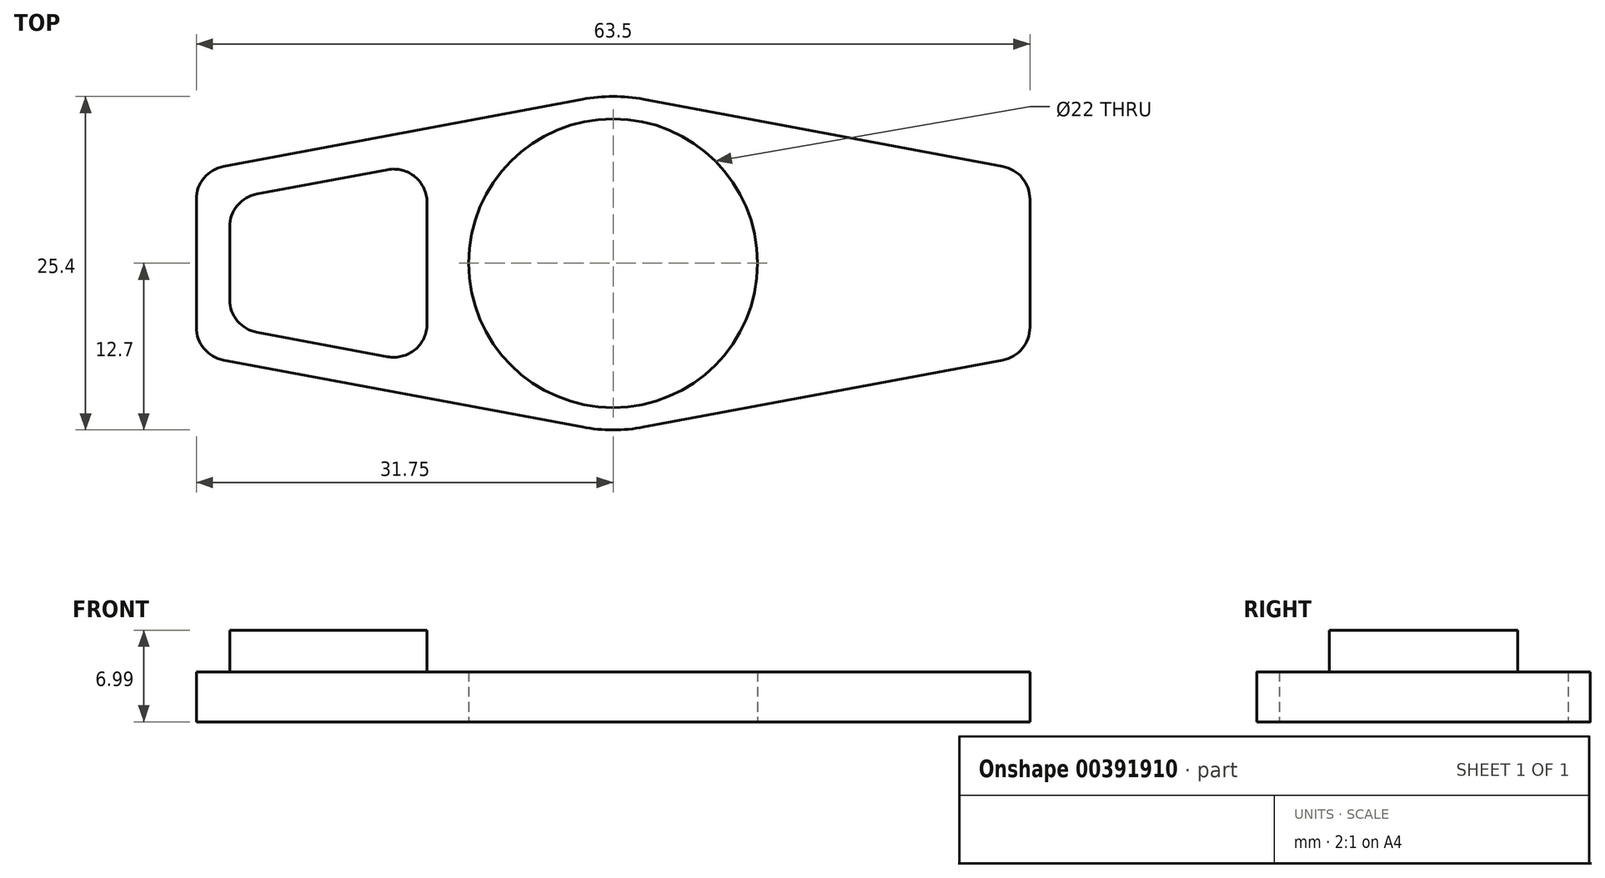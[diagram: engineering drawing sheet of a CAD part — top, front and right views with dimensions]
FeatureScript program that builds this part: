
annotation { "Feature Type Name" : "Feature", "Feature Type Description" : "" }
export const myFeature = defineFeature(function(context is Context, id is Id, definition is map)
    precondition{}
    {
        {
            var Q0;
            Q0=qCreatedBy(makeId("Top.planeOp"),FACE);
            var sketch = newSketch(context, id + "F0", { "sketchPlane" : qUnion([Q0])});
            skCircle(sketch, "E0", {"center": v(0, 0) * mm, "radius": 11 * mm});
            skArc(sketch, "E1", {"start": v(-2.33, -12.48) * mm, "mid": v(0, -12.7) * mm, "end": v(2.33, -12.48) * mm});
            skCircle(sketch, "E2", {"center": v(0, 0) * mm, "radius": 8 * mm, "construction": true});
            skLineSegment(sketch, "E3", {"start": v(2.33, 12.48) * mm, "end": v(31.75, 6.99) * mm});
            skLineSegment(sketch, "E4", {"start": v(31.75, 6.99) * mm, "end": v(31.75, -6.99) * mm});
            skLineSegment(sketch, "E5", {"start": v(31.75, -6.99) * mm, "end": v(2.33, -12.48) * mm});
            skLineSegment(sketch, "E6", {"start": v(0, 0) * mm, "end": v(73.48, 0) * mm, "construction": true});
            skLineSegment(sketch, "E7", {"start": v(0, 0) * mm, "end": v(0, 26.47) * mm, "construction": true});
            skLineSegment(sketch, "E8.MirrorCS", {"start": v(-31.75, -6.99) * mm, "end": v(-2.33, -12.48) * mm});
            skLineSegment(sketch, "E9.MirrorCS", {"start": v(-31.75, 6.99) * mm, "end": v(-31.75, -6.99) * mm});
            skLineSegment(sketch, "E10.MirrorCS", {"start": v(-2.33, 12.48) * mm, "end": v(-31.75, 6.99) * mm});
            skArc(sketch, "E11.trimOffspring", {"start": v(2.33, 12.48) * mm, "mid": v(0, 12.7) * mm, "end": v(-2.33, 12.48) * mm});
            skSolve(sketch);
        }
        {
            var Q0;
            Q0 = qSketchRegion(id + "F0", true);
            extrude(context, id + "F1", {"entities" : qUnion([Q0]), "endBound" : BoundingType.SYMMETRIC, "depth" : 3.8 * mm});
        }
        {
            var Q0;
            Q0=makeQuery(id+"F1.opExtrude","CAP_FACE",FACE,{"disambiguationData":[OSD([sQuery(id+"F0.wireOp",EDGE,"E0"),sQuery(id+"F0.wireOp",EDGE,"E1"),sQuery(id+"F0.wireOp",EDGE,"E3"),sQuery(id+"F0.wireOp",EDGE,"E4"),sQuery(id+"F0.wireOp",EDGE,"E5"),sQuery(id+"F0.wireOp",EDGE,"E8.MirrorCS"),sQuery(id+"F0.wireOp",EDGE,"E9.MirrorCS"),sQuery(id+"F0.wireOp",EDGE,"E10.MirrorCS"),sQuery(id+"F0.wireOp",EDGE,"E11.trimOffspring")])],"isStart":false});
            var sketch = newSketch(context, id + "F2", { "sketchPlane" : qUnion([Q0])});
            skLineSegment(sketch, "E12.0", {"start": v(-29.21, -4.88) * mm, "end": v(-14.17, -7.69) * mm});
            skLineSegment(sketch, "E12.1", {"start": v(-29.21, 4.88) * mm, "end": v(-29.21, -4.88) * mm});
            skLineSegment(sketch, "E12.2", {"start": v(-14.18, 7.69) * mm, "end": v(-29.21, 4.88) * mm});
            skLineSegment(sketch, "E13", {"start": v(-14.18, 7.69) * mm, "end": v(-14.17, -7.69) * mm});
            skSolve(sketch);
        }
        {
            var Q0;
            Q0=makeQuery(id+"F1.opExtrude","SWEPT_EDGE",EDGE,{"disambiguationData":[OSD([sQuery(id+"F0.wireOp",EDGE,"E9.MirrorCS"),sQuery(id+"F0.wireOp",EDGE,"E10.MirrorCS")])]});
            var Q1;
            Q1=makeQuery(id+"F1.opExtrude","SWEPT_EDGE",EDGE,{"disambiguationData":[OSD([sQuery(id+"F0.wireOp",EDGE,"E8.MirrorCS"),sQuery(id+"F0.wireOp",EDGE,"E9.MirrorCS")])]});
            var Q2;
            Q2=makeQuery(id+"F1.opExtrude","SWEPT_EDGE",EDGE,{"disambiguationData":[OSD([sQuery(id+"F0.wireOp",EDGE,"E4"),sQuery(id+"F0.wireOp",EDGE,"E5")])]});
            var Q3;
            Q3=makeQuery(id+"F1.opExtrude","SWEPT_EDGE",EDGE,{"disambiguationData":[OSD([sQuery(id+"F0.wireOp",EDGE,"E3"),sQuery(id+"F0.wireOp",EDGE,"E4")])]});
            fillet(context, id + "F3", {"entities" : qUnion([Q0, Q1, Q2, Q3]), "radius" : 2.54 * mm, "tangentPropagation" : true, "allowEdgeOverflow" : false});
        }
        {
            var Q0;
            Q0 = qSketchRegion(id + "F2", true);
            extrude(context, id + "F4", {"entities" : qUnion([Q0]), "operationType" : NewBodyOperationType.ADD, "depth" : 3.17 * mm});
        }
        {
            var Q0;
            Q0=makeQuery(id+"F4.opExtrude","SWEPT_EDGE",EDGE,{"disambiguationData":[OSD([sQuery(id+"F2.wireOp",EDGE,"E12.0"),sQuery(id+"F2.wireOp",EDGE,"E12.1")])]});
            var Q1;
            Q1=makeQuery(id+"F4.opExtrude","SWEPT_EDGE",EDGE,{"disambiguationData":[OSD([sQuery(id+"F2.wireOp",EDGE,"E12.0"),sQuery(id+"F2.wireOp",EDGE,"E13")])]});
            var Q2;
            Q2=makeQuery(id+"F4.opExtrude","SWEPT_EDGE",EDGE,{"disambiguationData":[OSD([sQuery(id+"F2.wireOp",EDGE,"E12.2"),sQuery(id+"F2.wireOp",EDGE,"E13")])]});
            var Q3;
            Q3=makeQuery(id+"F4.opExtrude","SWEPT_EDGE",EDGE,{"disambiguationData":[OSD([sQuery(id+"F2.wireOp",EDGE,"E12.1"),sQuery(id+"F2.wireOp",EDGE,"E12.2")])]});
            fillet(context, id + "F5", {"entities" : qUnion([Q0, Q1, Q2, Q3]), "radius" : 2.54 * mm, "tangentPropagation" : true, "allowEdgeOverflow" : false});
        }
    });
